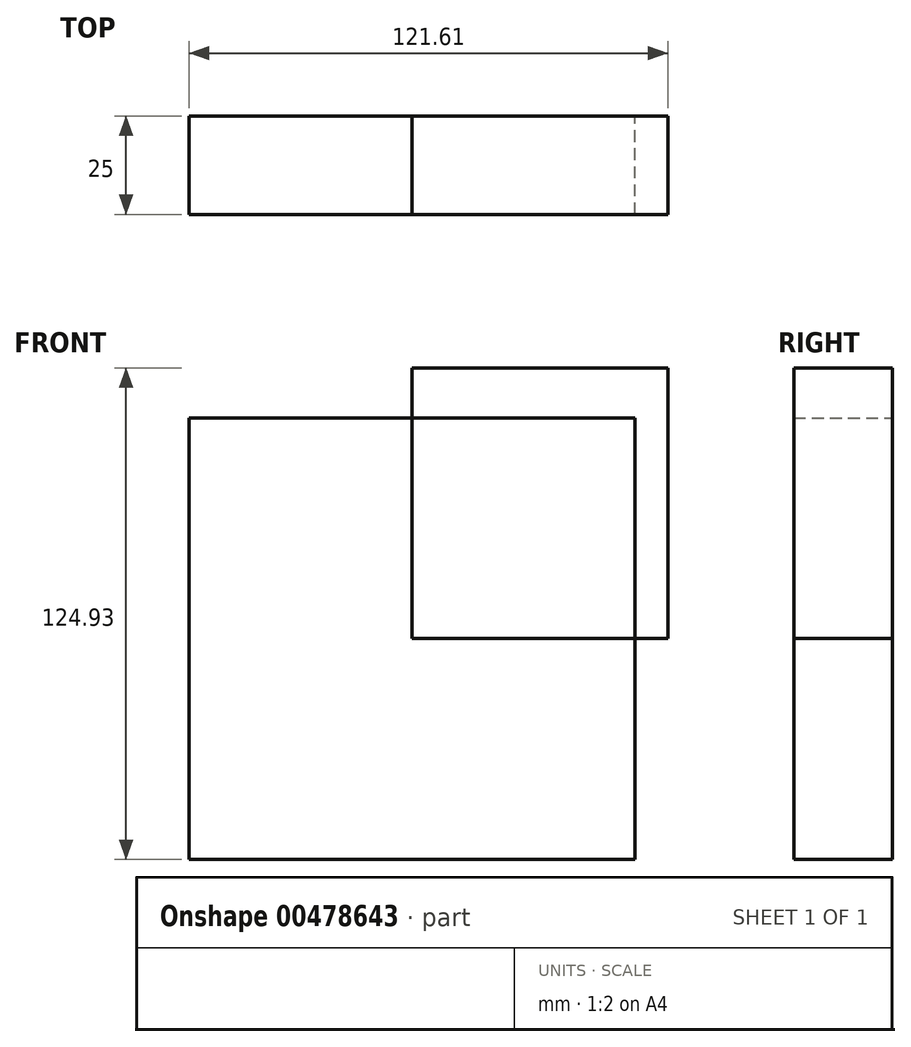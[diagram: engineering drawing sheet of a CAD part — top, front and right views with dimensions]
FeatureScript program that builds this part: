
annotation { "Feature Type Name" : "Feature", "Feature Type Description" : "" }
export const myFeature = defineFeature(function(context is Context, id is Id, definition is map)
    precondition{}
    {
        {
            var Q0;
            Q0=qCreatedBy(makeId("Front.planeOp"),FACE);
            var sketch = newSketch(context, id + "F0", { "sketchPlane" : qUnion([Q0])});
            skLineSegment(sketch, "E0.bottom", {"start": v(65, 68.8) * mm, "end": v(0, 68.8) * mm});
            skLineSegment(sketch, "E0.top", {"start": v(65, 0) * mm, "end": v(0, 0) * mm});
            skLineSegment(sketch, "E0.left", {"start": v(65, 68.8) * mm, "end": v(65, 0) * mm});
            skLineSegment(sketch, "E0.right", {"start": v(0, 68.8) * mm, "end": v(0, 0) * mm});
            skSolve(sketch);
        }
        {
            var Q0;
            Q0=makeQuery(id+"F0.imprint","IMPRINT",FACE,{"disambiguationData":[TD([[makeQuery(id+"F0.imprint","IMPRINT",EDGE,{"derivedFrom":sQuery(id+"F0.wireOp",EDGE,"E0.bottom")}),1.0]])]});
            extrude(context, id + "F1", {"entities" : qUnion([Q0]), "depth" : 25 * mm});
        }
        {
            var Q0;
            Q0=qCreatedBy(makeId("Front.planeOp"),FACE);
            var sketch = newSketch(context, id + "F2", { "sketchPlane" : qUnion([Q0])});
            skLineSegment(sketch, "E1.bottom", {"start": v(56.6, 56.12) * mm, "end": v(-56.6, 56.12) * mm});
            skLineSegment(sketch, "E1.top", {"start": v(56.6, -56.12) * mm, "end": v(-56.6, -56.12) * mm});
            skLineSegment(sketch, "E1.left", {"start": v(56.6, 56.12) * mm, "end": v(56.6, -56.12) * mm});
            skLineSegment(sketch, "E1.right", {"start": v(-56.6, 56.12) * mm, "end": v(-56.6, -56.12) * mm});
            skPoint(sketch, "E1.middle", {"position": v(0, 0) * mm});
            skSolve(sketch);
        }
        {
            var Q0;
            Q0=makeQuery(id+"F2.imprint","IMPRINT",FACE,{"disambiguationData":[TD([[makeQuery(id+"F2.imprint","IMPRINT",EDGE,{"derivedFrom":sQuery(id+"F2.wireOp",EDGE,"E1.bottom")}),1.0]])]});
            extrude(context, id + "F3", {"entities" : qUnion([Q0]), "depth" : 25 * mm});
        }
    });
